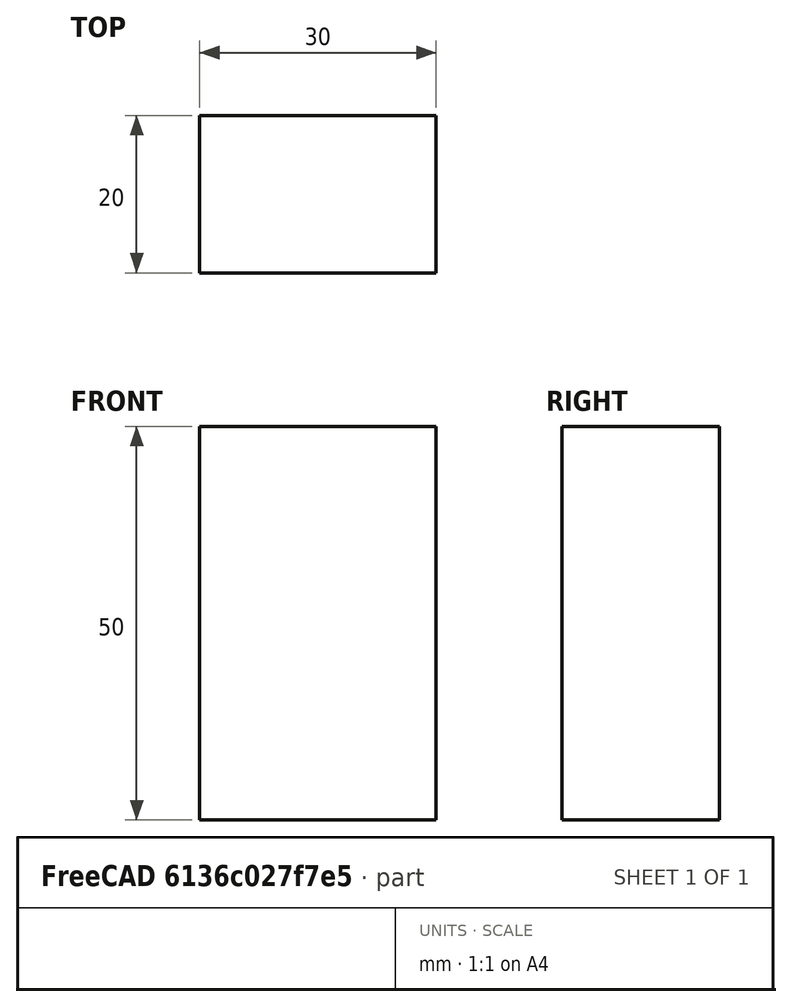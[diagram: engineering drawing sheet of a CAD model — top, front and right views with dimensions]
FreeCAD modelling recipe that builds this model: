
FCSTD DOCUMENT  (FreeCAD 0.15R4671 (Git))
Label: Flat Bar 30x20 EN10058 S235JR
License: All rights reserved
LicenseURL: http://en.wikipedia.org/wiki/All_rights_reserved
objects: Sketcher::SketchObject×1, Part::Extrusion×1
note: 2 computed .brp shape members not serialized (recipe doc carries the construction recipe); baked Part::Feature solids carry a one-line shape summary decoded from their .brp

FEATURE [Sketcher::SketchObject] Sketch
  sketch-geometry (4):
    g0: LineSegment StartX=-15 StartY=-10 StartZ=0 EndX=15 EndY=-10 EndZ=0
    g1: LineSegment StartX=15 StartY=-10 StartZ=0 EndX=15 EndY=10 EndZ=0
    g2: LineSegment StartX=15 StartY=10 StartZ=0 EndX=-15 EndY=10 EndZ=0
    g3: LineSegment StartX=-15 StartY=10 StartZ=0 EndX=-15 EndY=-10 EndZ=0
  constraints (12):
    c: Coincident(g0,g1)
    c: Coincident(g1,g2)
    c: Coincident(g2,g3)
    c: Coincident(g3,g0)
    c: Horizontal(g0)
    c: Horizontal(g2)
    c: Vertical(g1)
    c: Vertical(g3)
    c: Symmetric(g1,g2,g-2)
    c: Symmetric(g0,g1,g-1)
    c: DistanceY(g1) = 20
    c: DistanceX(g0) = 30
FEATURE [Part::Extrusion] Extrude  label="Flat Bar 30x20 EN10058 S235JR"
  Base = -> Sketch
  Dir = (0,0,50)
  Solid = true
